# Revit family: Fristående Värmelampa Exclusive
name_source: partatom
category: Lighting Fixtures
units: mm (PartAtom-declared; Revit-internal decimal feet)

## family parameters
Always vertical = Yes
Cut with Voids When Loaded = No
Light Source = No
OmniClass Number = 23.80.70.11
OmniClass Title = Luminaries for Internal Lighting
Part Type = Normal
Room Calculation Point = No
Round Connector Dimension = Use Diameter
Shared = No
Work Plane-Based = No

## types (6) — shared parameters
Bolt Material = AMA - Stainless Steel
Bracket Material = AMA - Black
Fot = 200 x 200 x 40 mm
Height = 700 mm  [stored 2.29659 ft]
Leg Material = AMA - Black
Light Material = AMA - Glass
Skärm = H 210 / Ø 180 mm
Switch Material = AMA - Black
Voltage = 230 V
Wattage = 250 W
zero-valued in all types: Default Elevation

## per-type parameters (varying)
| type | Fast Montering Option | Main Body Material | Montage med Tving Option | Standard Option |
| 24000-BS | No | AMA - Black | No | Yes |
| 24000-BV | No | AMA - White | No | Yes |
| 24000-BG | No | AMA - Brass | No | Yes |
| 24000-BC | No | AMA - Chromium | No | Yes |
| 24000-FC | Yes | AMA - Chromium | No | No |
| 24000-TC | No | AMA - Chromium | Yes | No |

note: column(s) folded — value = type name in every type: Artikelnummer

note: [stored X ft] marks values corroborated as IEEE doubles in the binary element streams (Revit-internal decimal feet)

## geometry (parser evidence)
native form markers: Sweep x8
no freeform markers — native parametric forms only
